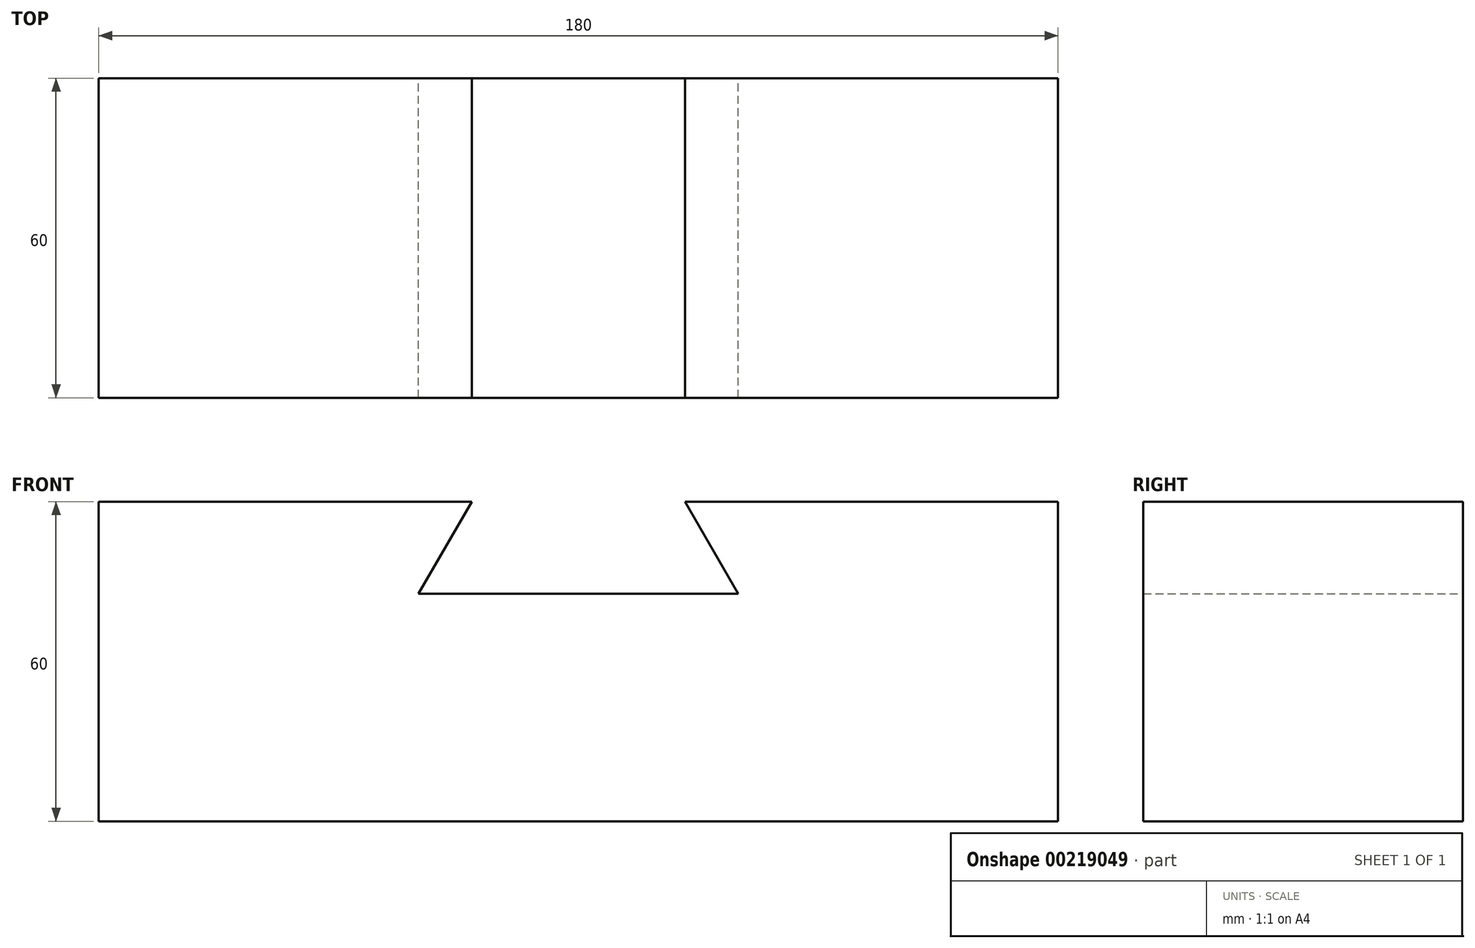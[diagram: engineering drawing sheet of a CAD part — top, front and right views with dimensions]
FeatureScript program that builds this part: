
annotation { "Feature Type Name" : "Feature", "Feature Type Description" : "" }
export const myFeature = defineFeature(function(context is Context, id is Id, definition is map)
    precondition{}
    {
        {
            var Q0;
            Q0=qCreatedBy(makeId("Front.planeOp"),FACE);
            var sketch = newSketch(context, id + "F0", { "sketchPlane" : qUnion([Q0])});
            skLineSegment(sketch, "E0", {"start": v(0, 0) * mm, "end": v(-90, 0) * mm});
            skLineSegment(sketch, "E1", {"start": v(-90, 0) * mm, "end": v(-90, 60) * mm});
            skLineSegment(sketch, "E2", {"start": v(-90, 60) * mm, "end": v(-20, 60) * mm});
            skLineSegment(sketch, "E3", {"start": v(-20, 60) * mm, "end": v(-30, 42.68) * mm});
            skLineSegment(sketch, "E4", {"start": v(-30, 42.68) * mm, "end": v(0, 42.68) * mm});
            skLineSegment(sketch, "E5", {"start": v(0, 42.68) * mm, "end": v(0, 0) * mm, "construction": true});
            skLineSegment(sketch, "E6.MirrorCS", {"start": v(90, 60) * mm, "end": v(20, 60) * mm});
            skLineSegment(sketch, "E7.MirrorCS", {"start": v(90, 0) * mm, "end": v(90, 60) * mm});
            skLineSegment(sketch, "E8.MirrorCS", {"start": v(0, 0) * mm, "end": v(90, 0) * mm});
            skLineSegment(sketch, "E9.MirrorCS", {"start": v(30, 42.68) * mm, "end": v(0, 42.68) * mm});
            skLineSegment(sketch, "E10.MirrorCS", {"start": v(20, 60) * mm, "end": v(30, 42.68) * mm});
            skSolve(sketch);
        }
        {
            var Q0;
            Q0 = qSketchRegion(id + "F0", true);
            extrude(context, id + "F1", {"entities" : qUnion([Q0]), "depth" : 60 * mm});
        }
    });
